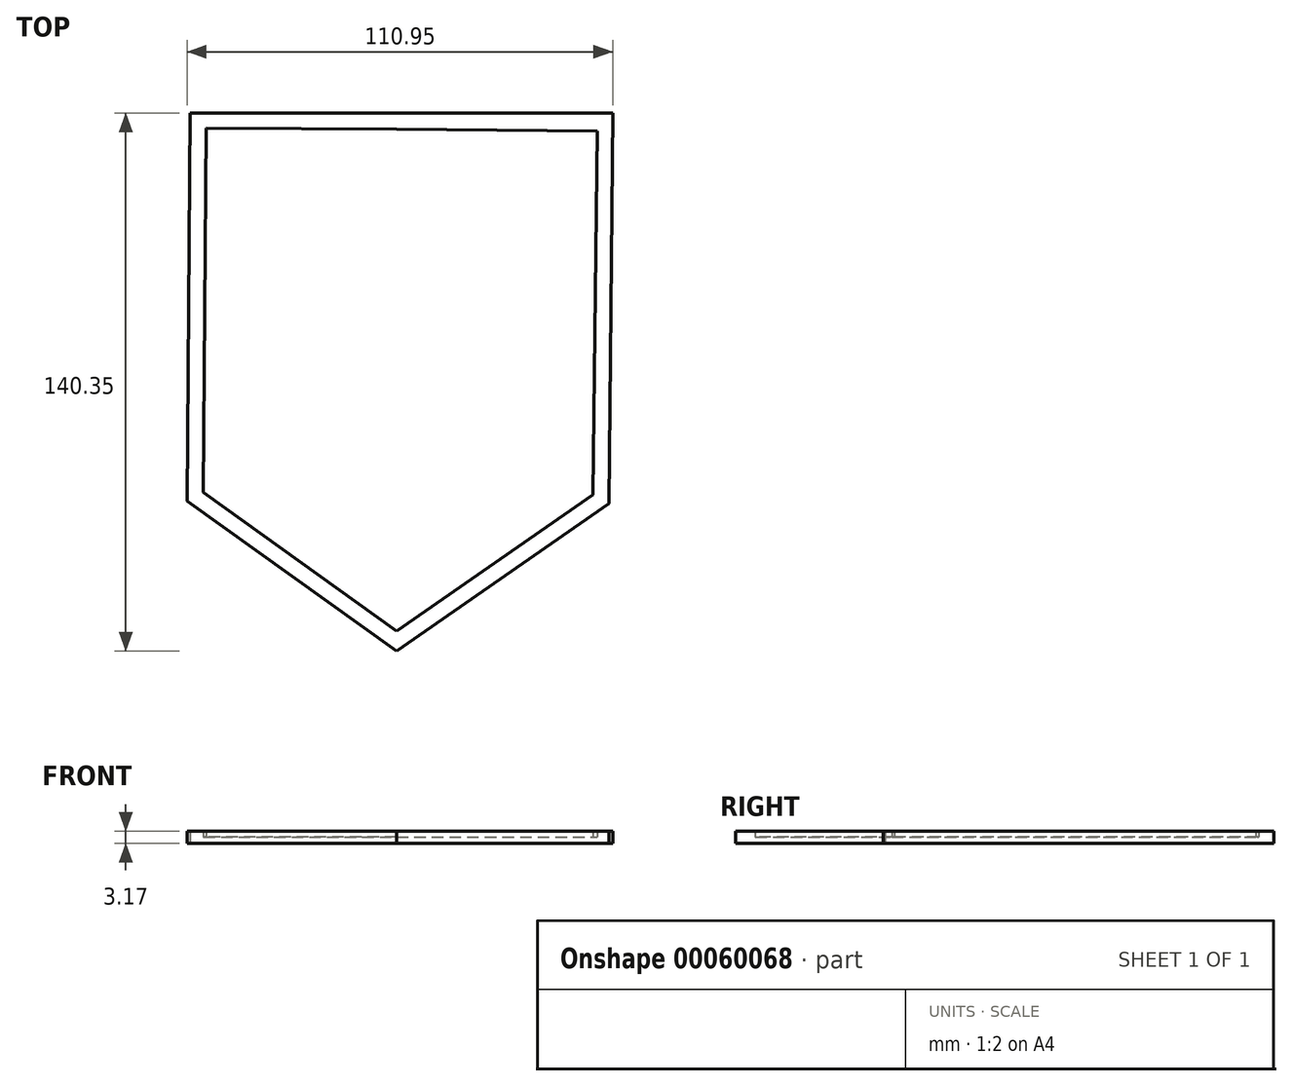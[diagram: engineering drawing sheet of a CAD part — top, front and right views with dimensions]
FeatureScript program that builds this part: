
annotation { "Feature Type Name" : "Feature", "Feature Type Description" : "" }
export const myFeature = defineFeature(function(context is Context, id is Id, definition is map)
    precondition{}
    {
        {
            var Q0;
            Q0=qCreatedBy(makeId("Top.planeOp"),FACE);
            var sketch = newSketch(context, id + "F0", { "sketchPlane" : qUnion([Q0])});
            skLineSegment(sketch, "E0", {"start": v(0, 65.12) * mm, "end": v(56.36, 65.12) * mm});
            skLineSegment(sketch, "E1", {"start": v(55.42, -36.73) * mm, "end": v(56.36, 65.12) * mm});
            skLineSegment(sketch, "E2", {"start": v(0, -75.23) * mm, "end": v(55.42, -36.73) * mm});
            skLineSegment(sketch, "E3", {"start": v(0, -70.05) * mm, "end": v(51.25, -34.45) * mm});
            skLineSegment(sketch, "E4", {"start": v(51.25, -34.45) * mm, "end": v(52.37, 60.42) * mm});
            skLineSegment(sketch, "E5", {"start": v(0, 60.9) * mm, "end": v(52.37, 60.42) * mm});
            skLineSegment(sketch, "E6", {"start": v(-44.54, 55.26) * mm, "end": v(46.04, 55.26) * mm});
            skLineSegment(sketch, "E7", {"start": v(46.04, 55.26) * mm, "end": v(45.56, -29.45) * mm});
            skLineSegment(sketch, "E8", {"start": v(-44.54, 55.26) * mm, "end": v(-45.2, -29.12) * mm});
            skLineSegment(sketch, "E9", {"start": v(-45.2, -29.12) * mm, "end": v(-38.68, -33.54) * mm});
            skFitSpline(sketch, "E10", {"points": [v(-38.62, -34.39) * mm, v(-39.34, -28.88) * mm, v(-40.21, -24.38) * mm, v(-40.45, -18.3) * mm, v(-40.74, -11.99) * mm, v(-40.5, -4.71) * mm, v(-39.57, 5.61) * mm, v(-35.35, 18.28) * mm, v(-30.65, 28.6) * mm, v(-25.72, 37.53) * mm, v(-21.03, 43.63) * mm, v(-18.68, 45.5) * mm, v(-15.87, 46.44) * mm, v(-8.36, 46.91) * mm, v(-3.9, 46.44) * mm, v(2.67, 44.57) * mm, v(6.19, 41.98) * mm, v(7.83, 39.4) * mm, v(9.48, 36.6) * mm, v(10.88, 37.53) * mm, v(12.06, 38.22) * mm, v(12.99, 37.53) * mm, v(13.46, 34.48) * mm, v(13.93, 31.43) * mm, v(15.1, 28.14) * mm, v(20.03, 26.03) * mm, v(25.43, 23.92) * mm, v(28.95, 22.27) * mm, v(32.47, 19.7) * mm, v(34.82, 16.64) * mm, v(36.7, 13.36) * mm, v(38.34, 10.77) * mm, v(38.8, 9.14) * mm, v(36.7, 9.84) * mm, v(31.77, 11.48) * mm, v(25.9, 13.83) * mm, v(18.63, 15.7) * mm, v(11.12, 17.11) * mm, v(4.08, 17.34) * mm, v(1.73, 16.88) * mm, v(-2.02, 15.23) * mm, v(-2.02, 12.18) * mm, v(-2.02, 9.13) * mm, v(2.2, 5.14) * mm, v(4.31, 3.97) * mm, v(7.83, 3.73) * mm, v(11.35, 3.03) * mm, v(14.64, 2.1) * mm, v(20.74, -2.37) * mm, v(24.73, -5.65) * mm, v(28.95, -9.64) * mm, v(32.94, -14.33) * mm, v(36.23, -18.32) * mm, v(38.8, -21.84) * mm, v(40.92, -25.36) * mm, v(42.56, -26.77) * mm, v(43.27, -29.45) * mm, v(45.56, -29.45) * mm], "startDerivative": vector(-10.99, 224.07) * mm, "endDerivative": vector(225.38, 57.8) * mm});
            skLineSegment(sketch, "E11", {"start": v(0, 65.12) * mm, "end": v(-53.89, 65.12) * mm});
            skLineSegment(sketch, "E12", {"start": v(-53.89, 65.12) * mm, "end": v(-54.59, -36.16) * mm});
            skLineSegment(sketch, "E13", {"start": v(-54.59, -36.16) * mm, "end": v(0, -75.23) * mm});
            skLineSegment(sketch, "E14", {"start": v(0, 60.9) * mm, "end": v(-49.66, 61.17) * mm});
            skLineSegment(sketch, "E15", {"start": v(-49.66, 61.17) * mm, "end": v(-50.37, -33.81) * mm});
            skLineSegment(sketch, "E16", {"start": v(-50.37, -33.81) * mm, "end": v(0, -70.05) * mm});
            skSolve(sketch);
        }
        {
            var Q0;
            Q0=makeQuery(id+"F0.imprint","IMPRINT",FACE,{"disambiguationData":[TD([[makeQuery(id+"F0.imprint","IMPRINT",EDGE,{"derivedFrom":sQuery(id+"F0.wireOp",EDGE,"E3")}),1.0]])]});
            var Q1;
            Q1=makeQuery(id+"F0.imprint","IMPRINT",FACE,{"disambiguationData":[TD([[makeQuery(id+"F0.imprint","IMPRINT",EDGE,{"derivedFrom":sQuery(id+"F0.wireOp",EDGE,"E6")}),-1.0]])]});
            extrude(context, id + "F1", {"entities" : qUnion([Q0, Q1]), "depth" : 1.59 * mm});
        }
        {
            var Q0;
            Q0=makeQuery(id+"F0.imprint","IMPRINT",FACE,{"disambiguationData":[TD([[makeQuery(id+"F0.imprint","IMPRINT",EDGE,{"derivedFrom":sQuery(id+"F0.wireOp",EDGE,"E0")}),-1.0]])]});
            extrude(context, id + "F2", {"entities" : qUnion([Q0]), "operationType" : NewBodyOperationType.ADD, "depth" : 3.17 * mm});
        }
    });
